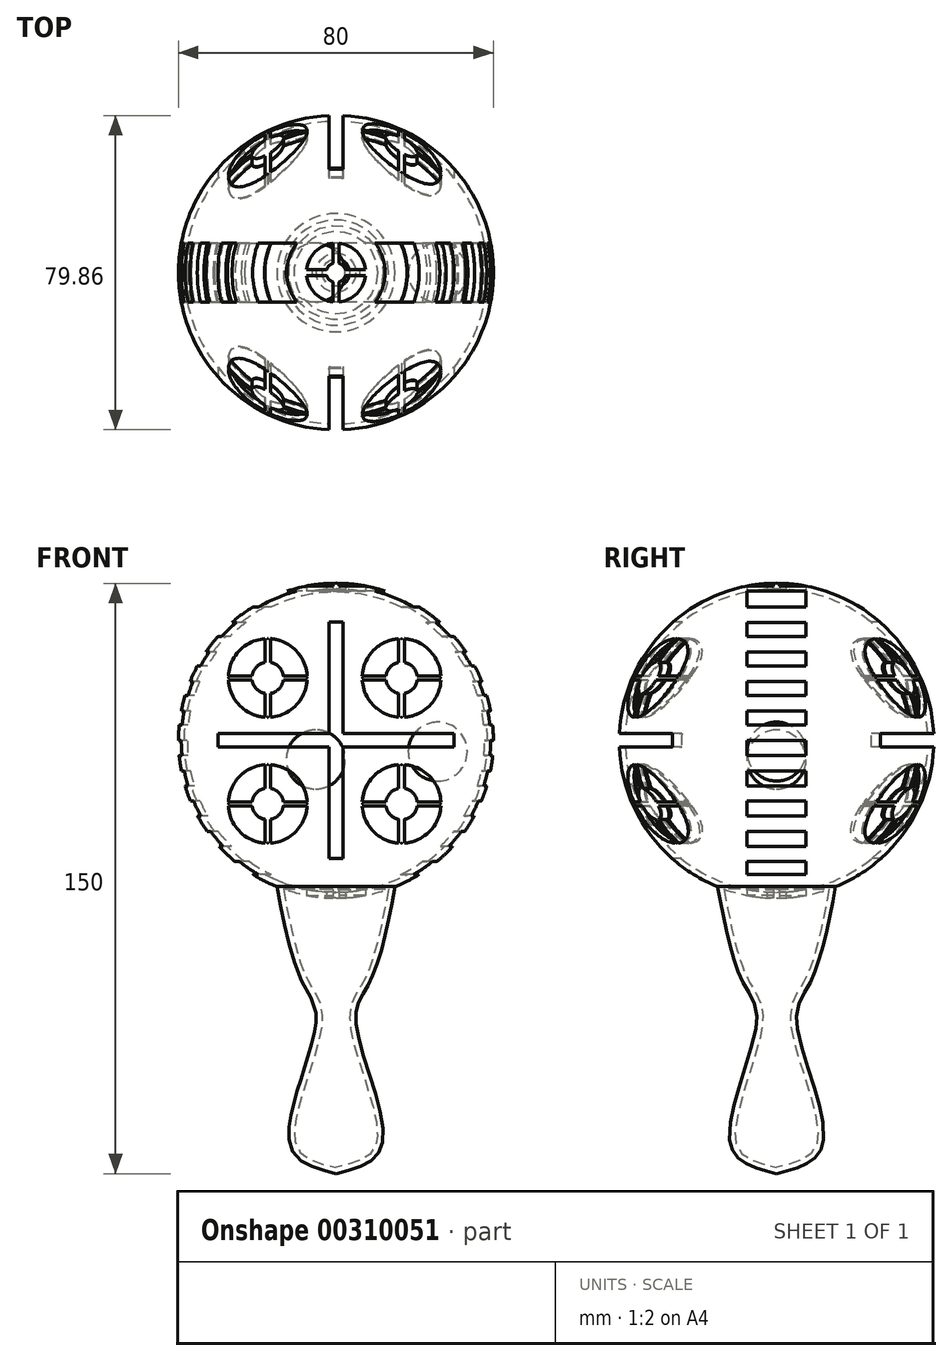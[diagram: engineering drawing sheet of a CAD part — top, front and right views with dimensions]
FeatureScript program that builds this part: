
annotation { "Feature Type Name" : "Feature", "Feature Type Description" : "" }
export const myFeature = defineFeature(function(context is Context, id is Id, definition is map)
    precondition{}
    {
        {
            var Q0;
            Q0=qCreatedBy(makeId("Front.planeOp"),FACE);
            var sketch = newSketch(context, id + "F0", { "sketchPlane" : qUnion([Q0])});
            skArc(sketch, "E0", {"start": v(0, 1.78) * mm, "mid": v(6.77, 2.36) * mm, "end": v(13.35, 4.08) * mm});
            skArc(sketch, "E1", {"start": v(0, 3.28) * mm, "mid": v(38.5, 41.78) * mm, "end": v(0, 80.28) * mm});
            skLineSegment(sketch, "E2", {"start": v(0, 81.78) * mm, "end": v(0, -68.22) * mm, "construction": true});
            skLineSegment(sketch, "E3", {"start": v(0, -68.22) * mm, "end": v(15, -68.22) * mm, "construction": true});
            skLineSegment(sketch, "E4", {"start": v(15, -68.22) * mm, "end": v(15, 6.32) * mm, "construction": true});
            skFitSpline(sketch, "E5", {"points": [v(15, 4.7) * mm, v(8.78, -19.12) * mm, v(5.03, -29.47) * mm, v(11.76, -60.64) * mm, v(0, -68.22) * mm], "startDerivative": vector(-18.71, -98) * mm, "endDerivative": vector(-75.4, -18.66) * mm});
            skFitSpline(sketch, "E6.0", {"points": [v(13.53, 4.98) * mm, v(13.14, 2.94) * mm, v(12.36, -1.13) * mm, v(11.34, -6) * mm, v(10.46, -9.63) * mm, v(9.77, -12.19) * mm, v(9.04, -14.55) * mm, v(8.4, -16.32) * mm, v(7.85, -17.6) * mm, v(7.43, -18.49) * mm, v(7, -19.31) * mm, v(6.4, -20.37) * mm, v(5.63, -21.64) * mm, v(4.74, -23.24) * mm, v(3.99, -25.03) * mm, v(3.6, -26.77) * mm, v(3.5, -28.31) * mm, v(3.52, -29.56) * mm, v(3.66, -30.9) * mm, v(3.98, -32.76) * mm, v(4.57, -35.27) * mm, v(5.51, -38.5) * mm, v(6.58, -41.88) * mm, v(7.68, -45.32) * mm, v(8.72, -48.72) * mm, v(9.61, -52) * mm, v(10.25, -55.06) * mm, v(10.55, -57.77) * mm, v(10.46, -59.63) * mm, v(10.19, -60.8) * mm, v(9.78, -61.81) * mm, v(9.05, -62.86) * mm, v(7.79, -63.92) * mm, v(6.14, -64.81) * mm, v(4.17, -65.55) * mm, v(1.98, -66.18) * mm, v(0.42, -66.57) * mm, v(-0.36, -66.76) * mm]});
            skLineSegment(sketch, "E7", {"start": v(0, -68.22) * mm, "end": v(0, 3.28) * mm});
            skArc(sketch, "E8.trimOffspring", {"start": v(15, 4.7) * mm, "mid": v(39.26, 49.42) * mm, "end": v(0, 81.78) * mm});
            skLineSegment(sketch, "E9", {"start": v(0, 81.78) * mm, "end": v(0, 80.28) * mm});
            skLineSegment(sketch, "E10", {"start": v(40, 41.95) * mm, "end": v(0, 41.78) * mm, "construction": true});
            skSolve(sketch);
        }
        {
            var Q0;
            {var subQ3=sQuery(id+"F0.wireOp",EDGE,"E0");Q0=makeQuery(id+"F0.imprint","IMPRINT",FACE,{"disambiguationData":[TD([[makeQuery(id+"F0.imprint","IMPRINT",EDGE,{"derivedFrom":subQ3}),1.0]])]});}
            var Q1;
            Q1=sQuery(id+"F0.wireOp",EDGE,"E2");
            revolve(context, id + "F1", {"entities" : qUnion([Q0]), "axis" : qUnion([Q1]), "revolveType" : RevolveType.FULL});
        }
        {
            var Q0;
            Q0=qCreatedBy(makeId("Front.planeOp"),FACE);
            var sketch = newSketch(context, id + "F2", { "sketchPlane" : qUnion([Q0])});
            skArc(sketch, "E11", {"start": v(15.94, 35.7) * mm, "mid": v(9.52, 32.73) * mm, "end": v(6.68, 26.25) * mm});
            skLineSegment(sketch, "E12", {"start": v(16.67, 35.73) * mm, "end": v(16.67, 35.7) * mm});
            skLineSegment(sketch, "E13", {"start": v(16.67, 15.73) * mm, "end": v(16.7, 15.76) * mm});
            skLineSegment(sketch, "E14", {"start": v(6.67, 25.73) * mm, "end": v(6.68, 25.74) * mm});
            skLineSegment(sketch, "E15", {"start": v(26.67, 25.73) * mm, "end": v(26.66, 25.74) * mm});
            skLineSegment(sketch, "E16", {"start": v(16.67, 15.73) * mm, "end": v(16.64, 15.76) * mm});
            skLineSegment(sketch, "E17.left", {"start": v(6.68, 25.72) * mm, "end": v(6.68, 25.74) * mm});
            skLineSegment(sketch, "E17.right", {"start": v(26.66, 25.72) * mm, "end": v(26.66, 25.74) * mm});
            skLineSegment(sketch, "E18.trimOffspring", {"start": v(6.68, 25.72) * mm, "end": v(6.67, 25.73) * mm});
            skLineSegment(sketch, "E19.trimOffspring", {"start": v(26.66, 25.72) * mm, "end": v(26.67, 25.73) * mm});
            skLineSegment(sketch, "E20.bottom", {"start": v(16.64, 15.76) * mm, "end": v(16.7, 15.76) * mm});
            skLineSegment(sketch, "E20.top", {"start": v(16.64, 35.7) * mm, "end": v(16.7, 35.7) * mm});
            skLineSegment(sketch, "E21.trimOffspring", {"start": v(16.64, 35.7) * mm, "end": v(16.67, 35.73) * mm});
            skLineSegment(sketch, "E22.trimOffspring", {"start": v(16.7, 35.7) * mm, "end": v(16.67, 35.73) * mm});
            skLineSegment(sketch, "E23.trimOffspring", {"start": v(16.67, 15.76) * mm, "end": v(16.67, 15.73) * mm});
            skLineSegment(sketch, "E24.bottom", {"start": v(-30, 40.15) * mm, "end": v(-1.75, 40.15) * mm});
            skLineSegment(sketch, "E24.top", {"start": v(-30, 43.65) * mm, "end": v(-1.75, 43.65) * mm});
            skLineSegment(sketch, "E24.left", {"start": v(-30, 40.15) * mm, "end": v(-30, 43.65) * mm});
            skLineSegment(sketch, "E24.right", {"start": v(30, 40.15) * mm, "end": v(30, 43.65) * mm});
            skPoint(sketch, "E24.middle", {"position": v(0, 41.9) * mm});
            skLineSegment(sketch, "E25.bottom", {"start": v(-1.75, 11.9) * mm, "end": v(1.75, 11.9) * mm});
            skLineSegment(sketch, "E25.top", {"start": v(-1.75, 71.9) * mm, "end": v(1.75, 71.9) * mm});
            skLineSegment(sketch, "E25.left", {"start": v(-1.75, 11.9) * mm, "end": v(-1.75, 40.15) * mm});
            skLineSegment(sketch, "E25.right", {"start": v(1.75, 11.9) * mm, "end": v(1.75, 40.15) * mm});
            skLineSegment(sketch, "E26.trimOffspring", {"start": v(1.75, 43.65) * mm, "end": v(1.75, 71.9) * mm});
            skLineSegment(sketch, "E27.trimOffspring", {"start": v(1.75, 43.65) * mm, "end": v(30, 43.65) * mm});
            skLineSegment(sketch, "E28.trimOffspring", {"start": v(1.75, 40.15) * mm, "end": v(30, 40.15) * mm});
            skLineSegment(sketch, "E29.trimOffspring", {"start": v(-1.75, 43.65) * mm, "end": v(-1.75, 71.9) * mm});
            skLineSegment(sketch, "E30.bottom", {"start": v(15.94, 37.7) * mm, "end": v(17.4, 37.7) * mm});
            skLineSegment(sketch, "E30.left", {"start": v(15.94, 35.7) * mm, "end": v(15.94, 29.66) * mm});
            skLineSegment(sketch, "E30.right", {"start": v(17.4, 35.7) * mm, "end": v(17.4, 29.66) * mm});
            skLineSegment(sketch, "E31.bottom", {"start": v(6.68, 26.25) * mm, "end": v(12.7, 26.25) * mm});
            skLineSegment(sketch, "E31.top", {"start": v(6.68, 25.21) * mm, "end": v(12.7, 25.21) * mm});
            skArc(sketch, "E32", {"start": v(12.7, 25.21) * mm, "mid": v(13.77, 22.98) * mm, "end": v(15.94, 21.8) * mm});
            skLineSegment(sketch, "E33.trimOffspring", {"start": v(20.64, 26.25) * mm, "end": v(26.66, 26.25) * mm});
            skLineSegment(sketch, "E34.trimOffspring", {"start": v(20.64, 25.21) * mm, "end": v(26.66, 25.21) * mm});
            skLineSegment(sketch, "E35.trimOffspring", {"start": v(17.4, 21.8) * mm, "end": v(17.4, 15.76) * mm});
            skLineSegment(sketch, "E36.trimOffspring", {"start": v(15.94, 21.8) * mm, "end": v(15.94, 15.76) * mm});
            skArc(sketch, "E37.trimOffspring", {"start": v(15.94, 29.66) * mm, "mid": v(13.77, 28.48) * mm, "end": v(12.7, 26.25) * mm});
            skArc(sketch, "E38.trimOffspring", {"start": v(20.64, 26.25) * mm, "mid": v(19.57, 28.48) * mm, "end": v(17.4, 29.66) * mm});
            skArc(sketch, "E39.trimOffspring", {"start": v(17.4, 21.8) * mm, "mid": v(19.57, 22.98) * mm, "end": v(20.64, 25.21) * mm});
            skArc(sketch, "E40.trimOffspring", {"start": v(26.66, 26.25) * mm, "mid": v(23.82, 32.73) * mm, "end": v(17.4, 35.7) * mm});
            skArc(sketch, "E41.trimOffspring", {"start": v(6.68, 25.21) * mm, "mid": v(9.52, 18.74) * mm, "end": v(15.94, 15.76) * mm});
            skArc(sketch, "E42.trimOffspring", {"start": v(17.4, 15.76) * mm, "mid": v(23.82, 18.74) * mm, "end": v(26.66, 25.21) * mm});
            skLineSegment(sketch, "E43.0.1.0", {"start": v(17.4, 67.7) * mm, "end": v(17.4, 61.66) * mm});
            skArc(sketch, "E43.0.1.1", {"start": v(17.4, 47.76) * mm, "mid": v(23.82, 50.74) * mm, "end": v(26.66, 57.21) * mm});
            skArc(sketch, "E43.0.1.2", {"start": v(6.68, 57.21) * mm, "mid": v(9.52, 50.74) * mm, "end": v(15.94, 47.76) * mm});
            skLineSegment(sketch, "E43.0.1.3", {"start": v(17.4, 53.8) * mm, "end": v(17.4, 47.76) * mm});
            skLineSegment(sketch, "E43.0.1.4", {"start": v(6.68, 58.25) * mm, "end": v(12.7, 58.25) * mm});
            skPoint(sketch, "E43.0.1.5", {"position": v(16.67, 57.73) * mm});
            skLineSegment(sketch, "E43.0.1.6", {"start": v(6.68, 57.21) * mm, "end": v(12.7, 57.21) * mm});
            skArc(sketch, "E43.0.1.7", {"start": v(15.94, 61.66) * mm, "mid": v(13.77, 60.48) * mm, "end": v(12.7, 58.25) * mm});
            skArc(sketch, "E43.0.1.8", {"start": v(15.94, 67.7) * mm, "mid": v(9.52, 64.73) * mm, "end": v(6.68, 58.25) * mm});
            skLineSegment(sketch, "E43.0.1.10", {"start": v(15.94, 67.7) * mm, "end": v(15.94, 61.66) * mm});
            skArc(sketch, "E43.0.1.11", {"start": v(26.66, 58.25) * mm, "mid": v(23.82, 64.73) * mm, "end": v(17.4, 67.7) * mm});
            skLineSegment(sketch, "E43.0.1.12", {"start": v(15.94, 53.8) * mm, "end": v(15.94, 47.76) * mm});
            skPoint(sketch, "E43.0.1.13", {"position": v(16.67, 57.73) * mm});
            skLineSegment(sketch, "E43.0.1.14", {"start": v(20.64, 58.25) * mm, "end": v(26.66, 58.25) * mm});
            skLineSegment(sketch, "E43.0.1.17", {"start": v(20.64, 57.21) * mm, "end": v(26.66, 57.21) * mm});
            skArc(sketch, "E43.0.1.18", {"start": v(17.4, 53.8) * mm, "mid": v(19.57, 54.98) * mm, "end": v(20.64, 57.21) * mm});
            skPoint(sketch, "E43.0.1.19", {"position": v(16.67, 57.73) * mm});
            skArc(sketch, "E43.0.1.20", {"start": v(12.7, 57.21) * mm, "mid": v(13.77, 54.98) * mm, "end": v(15.94, 53.8) * mm});
            skArc(sketch, "E43.0.1.21", {"start": v(20.64, 58.25) * mm, "mid": v(19.57, 60.48) * mm, "end": v(17.4, 61.66) * mm});
            skPoint(sketch, "E43.0.1.22", {"position": v(16.67, 57.73) * mm});
            skLineSegment(sketch, "E43.0.1.23", {"start": v(26.66, 57.72) * mm, "end": v(26.67, 57.73) * mm});
            skLineSegment(sketch, "E43.0.1.24", {"start": v(6.68, 57.72) * mm, "end": v(6.67, 57.73) * mm});
            skLineSegment(sketch, "E43.0.1.25", {"start": v(6.68, 57.72) * mm, "end": v(6.68, 57.74) * mm});
            skLineSegment(sketch, "E43.0.1.26", {"start": v(26.66, 57.72) * mm, "end": v(26.66, 57.74) * mm});
            skLineSegment(sketch, "E43.0.1.27", {"start": v(6.67, 57.73) * mm, "end": v(6.68, 57.74) * mm});
            skLineSegment(sketch, "E43.0.1.28", {"start": v(26.67, 57.73) * mm, "end": v(26.66, 57.74) * mm});
            skLineSegment(sketch, "E43.0.1.29", {"start": v(15.94, 45.75) * mm, "end": v(17.4, 45.75) * mm});
            skLineSegment(sketch, "E43.0.1.30", {"start": v(16.64, 67.7) * mm, "end": v(16.67, 67.73) * mm});
            skLineSegment(sketch, "E43.0.1.31", {"start": v(16.64, 47.76) * mm, "end": v(16.7, 47.76) * mm});
            skLineSegment(sketch, "E43.0.1.32", {"start": v(16.67, 47.73) * mm, "end": v(16.64, 47.76) * mm});
            skLineSegment(sketch, "E43.0.1.33", {"start": v(16.64, 67.7) * mm, "end": v(16.7, 67.7) * mm});
            skLineSegment(sketch, "E43.0.1.34", {"start": v(16.67, 47.73) * mm, "end": v(16.7, 47.76) * mm});
            skLineSegment(sketch, "E43.0.1.35", {"start": v(16.67, 67.73) * mm, "end": v(16.67, 67.7) * mm});
            skLineSegment(sketch, "E43.0.1.36", {"start": v(16.67, 47.76) * mm, "end": v(16.67, 47.73) * mm});
            skLineSegment(sketch, "E43.0.1.37", {"start": v(16.7, 67.7) * mm, "end": v(16.67, 67.73) * mm});
            skLineSegment(sketch, "E43.1.0.0", {"start": v(-16.6, 35.7) * mm, "end": v(-16.6, 29.66) * mm});
            skArc(sketch, "E43.1.0.1", {"start": v(-16.6, 15.76) * mm, "mid": v(-10.18, 18.74) * mm, "end": v(-7.34, 25.21) * mm});
            skArc(sketch, "E43.1.0.2", {"start": v(-27.32, 25.21) * mm, "mid": v(-24.48, 18.74) * mm, "end": v(-18.06, 15.76) * mm});
            skLineSegment(sketch, "E43.1.0.3", {"start": v(-16.6, 21.8) * mm, "end": v(-16.6, 15.76) * mm});
            skLineSegment(sketch, "E43.1.0.4", {"start": v(-27.32, 26.25) * mm, "end": v(-21.3, 26.25) * mm});
            skPoint(sketch, "E43.1.0.5", {"position": v(-17.33, 25.73) * mm});
            skLineSegment(sketch, "E43.1.0.6", {"start": v(-27.32, 25.21) * mm, "end": v(-21.3, 25.21) * mm});
            skArc(sketch, "E43.1.0.7", {"start": v(-18.06, 29.66) * mm, "mid": v(-20.23, 28.48) * mm, "end": v(-21.3, 26.25) * mm});
            skArc(sketch, "E43.1.0.8", {"start": v(-18.06, 35.7) * mm, "mid": v(-24.48, 32.73) * mm, "end": v(-27.32, 26.25) * mm});
            skLineSegment(sketch, "E43.1.0.10", {"start": v(-18.06, 35.7) * mm, "end": v(-18.06, 29.66) * mm});
            skArc(sketch, "E43.1.0.11", {"start": v(-7.34, 26.25) * mm, "mid": v(-10.18, 32.73) * mm, "end": v(-16.6, 35.7) * mm});
            skLineSegment(sketch, "E43.1.0.12", {"start": v(-18.06, 21.8) * mm, "end": v(-18.06, 15.76) * mm});
            skPoint(sketch, "E43.1.0.13", {"position": v(-17.33, 25.73) * mm});
            skLineSegment(sketch, "E43.1.0.14", {"start": v(-13.36, 26.25) * mm, "end": v(-7.34, 26.25) * mm});
            skLineSegment(sketch, "E43.1.0.17", {"start": v(-13.36, 25.21) * mm, "end": v(-7.34, 25.21) * mm});
            skArc(sketch, "E43.1.0.18", {"start": v(-16.6, 21.8) * mm, "mid": v(-14.43, 22.98) * mm, "end": v(-13.36, 25.21) * mm});
            skPoint(sketch, "E43.1.0.19", {"position": v(-17.33, 25.73) * mm});
            skArc(sketch, "E43.1.0.20", {"start": v(-21.3, 25.21) * mm, "mid": v(-20.23, 22.98) * mm, "end": v(-18.06, 21.8) * mm});
            skArc(sketch, "E43.1.0.21", {"start": v(-13.36, 26.25) * mm, "mid": v(-14.43, 28.48) * mm, "end": v(-16.6, 29.66) * mm});
            skPoint(sketch, "E43.1.0.22", {"position": v(-17.33, 25.73) * mm});
            skLineSegment(sketch, "E43.1.0.23", {"start": v(-7.34, 25.72) * mm, "end": v(-7.33, 25.73) * mm});
            skLineSegment(sketch, "E43.1.0.24", {"start": v(-27.32, 25.72) * mm, "end": v(-27.33, 25.73) * mm});
            skLineSegment(sketch, "E43.1.0.25", {"start": v(-27.32, 25.72) * mm, "end": v(-27.32, 25.74) * mm});
            skLineSegment(sketch, "E43.1.0.26", {"start": v(-7.34, 25.72) * mm, "end": v(-7.34, 25.74) * mm});
            skLineSegment(sketch, "E43.1.0.27", {"start": v(-27.33, 25.73) * mm, "end": v(-27.32, 25.74) * mm});
            skLineSegment(sketch, "E43.1.0.28", {"start": v(-7.33, 25.73) * mm, "end": v(-7.34, 25.74) * mm});
            skLineSegment(sketch, "E43.1.0.30", {"start": v(-17.36, 35.7) * mm, "end": v(-17.33, 35.73) * mm});
            skLineSegment(sketch, "E43.1.0.31", {"start": v(-17.36, 15.76) * mm, "end": v(-17.3, 15.76) * mm});
            skLineSegment(sketch, "E43.1.0.32", {"start": v(-17.33, 15.73) * mm, "end": v(-17.36, 15.76) * mm});
            skLineSegment(sketch, "E43.1.0.33", {"start": v(-17.36, 35.7) * mm, "end": v(-17.3, 35.7) * mm});
            skLineSegment(sketch, "E43.1.0.34", {"start": v(-17.33, 15.73) * mm, "end": v(-17.3, 15.76) * mm});
            skLineSegment(sketch, "E43.1.0.35", {"start": v(-17.33, 35.73) * mm, "end": v(-17.33, 35.7) * mm});
            skLineSegment(sketch, "E43.1.0.36", {"start": v(-17.33, 15.76) * mm, "end": v(-17.33, 15.73) * mm});
            skLineSegment(sketch, "E43.1.0.37", {"start": v(-17.3, 35.7) * mm, "end": v(-17.33, 35.73) * mm});
            skLineSegment(sketch, "E43.1.1.0", {"start": v(-16.6, 67.7) * mm, "end": v(-16.6, 61.66) * mm});
            skArc(sketch, "E43.1.1.1", {"start": v(-16.6, 47.76) * mm, "mid": v(-10.18, 50.74) * mm, "end": v(-7.34, 57.21) * mm});
            skArc(sketch, "E43.1.1.2", {"start": v(-27.32, 57.21) * mm, "mid": v(-24.48, 50.74) * mm, "end": v(-18.06, 47.76) * mm});
            skLineSegment(sketch, "E43.1.1.3", {"start": v(-16.6, 53.8) * mm, "end": v(-16.6, 47.76) * mm});
            skLineSegment(sketch, "E43.1.1.4", {"start": v(-27.32, 58.25) * mm, "end": v(-21.3, 58.25) * mm});
            skPoint(sketch, "E43.1.1.5", {"position": v(-17.33, 57.73) * mm});
            skLineSegment(sketch, "E43.1.1.6", {"start": v(-27.32, 57.21) * mm, "end": v(-21.3, 57.21) * mm});
            skArc(sketch, "E43.1.1.7", {"start": v(-18.06, 61.66) * mm, "mid": v(-20.23, 60.48) * mm, "end": v(-21.3, 58.25) * mm});
            skArc(sketch, "E43.1.1.8", {"start": v(-18.06, 67.7) * mm, "mid": v(-24.48, 64.73) * mm, "end": v(-27.32, 58.25) * mm});
            skLineSegment(sketch, "E43.1.1.10", {"start": v(-18.06, 67.7) * mm, "end": v(-18.06, 61.66) * mm});
            skArc(sketch, "E43.1.1.11", {"start": v(-7.34, 58.25) * mm, "mid": v(-10.18, 64.73) * mm, "end": v(-16.6, 67.7) * mm});
            skLineSegment(sketch, "E43.1.1.12", {"start": v(-18.06, 53.8) * mm, "end": v(-18.06, 47.76) * mm});
            skPoint(sketch, "E43.1.1.13", {"position": v(-17.33, 57.73) * mm});
            skLineSegment(sketch, "E43.1.1.14", {"start": v(-13.36, 58.25) * mm, "end": v(-7.34, 58.25) * mm});
            skLineSegment(sketch, "E43.1.1.17", {"start": v(-13.36, 57.21) * mm, "end": v(-7.34, 57.21) * mm});
            skArc(sketch, "E43.1.1.18", {"start": v(-16.6, 53.8) * mm, "mid": v(-14.43, 54.98) * mm, "end": v(-13.36, 57.21) * mm});
            skPoint(sketch, "E43.1.1.19", {"position": v(-17.33, 57.73) * mm});
            skArc(sketch, "E43.1.1.20", {"start": v(-21.3, 57.21) * mm, "mid": v(-20.23, 54.98) * mm, "end": v(-18.06, 53.8) * mm});
            skArc(sketch, "E43.1.1.21", {"start": v(-13.36, 58.25) * mm, "mid": v(-14.43, 60.48) * mm, "end": v(-16.6, 61.66) * mm});
            skPoint(sketch, "E43.1.1.22", {"position": v(-17.33, 57.73) * mm});
            skLineSegment(sketch, "E43.1.1.23", {"start": v(-7.34, 57.72) * mm, "end": v(-7.33, 57.73) * mm});
            skLineSegment(sketch, "E43.1.1.24", {"start": v(-27.32, 57.72) * mm, "end": v(-27.33, 57.73) * mm});
            skLineSegment(sketch, "E43.1.1.25", {"start": v(-27.32, 57.72) * mm, "end": v(-27.32, 57.74) * mm});
            skLineSegment(sketch, "E43.1.1.26", {"start": v(-7.34, 57.72) * mm, "end": v(-7.34, 57.74) * mm});
            skLineSegment(sketch, "E43.1.1.27", {"start": v(-27.33, 57.73) * mm, "end": v(-27.32, 57.74) * mm});
            skLineSegment(sketch, "E43.1.1.28", {"start": v(-7.33, 57.73) * mm, "end": v(-7.34, 57.74) * mm});
            skLineSegment(sketch, "E43.1.1.30", {"start": v(-17.36, 67.7) * mm, "end": v(-17.33, 67.73) * mm});
            skLineSegment(sketch, "E43.1.1.31", {"start": v(-17.36, 47.76) * mm, "end": v(-17.3, 47.76) * mm});
            skLineSegment(sketch, "E43.1.1.32", {"start": v(-17.33, 47.73) * mm, "end": v(-17.36, 47.76) * mm});
            skLineSegment(sketch, "E43.1.1.33", {"start": v(-17.36, 67.7) * mm, "end": v(-17.3, 67.7) * mm});
            skLineSegment(sketch, "E43.1.1.34", {"start": v(-17.33, 47.73) * mm, "end": v(-17.3, 47.76) * mm});
            skLineSegment(sketch, "E43.1.1.35", {"start": v(-17.33, 67.73) * mm, "end": v(-17.33, 67.7) * mm});
            skLineSegment(sketch, "E43.1.1.36", {"start": v(-17.33, 47.76) * mm, "end": v(-17.33, 47.73) * mm});
            skLineSegment(sketch, "E43.1.1.37", {"start": v(-17.3, 67.7) * mm, "end": v(-17.33, 67.73) * mm});
            skLineSegment(sketch, "E43.direction1", {"start": v(15.94, 13.75) * mm, "end": v(-18.06, 13.75) * mm, "construction": true});
            skLineSegment(sketch, "E43.direction2", {"start": v(15.94, 13.75) * mm, "end": v(15.94, 45.75) * mm, "construction": true});
            skSolve(sketch);
        }
        {
            var Q0;
            Q0 = qSketchRegion(id + "F2", true);
            extrude(context, id + "F3", {"entities" : qUnion([Q0]), "operationType" : NewBodyOperationType.REMOVE, "endBound" : BoundingType.SYMMETRIC, "oppositeDirection" : true, "depth" : 85 * mm});
        }
        {
            var Q0;
            Q0=qCreatedBy(makeId("Right.planeOp"),FACE);
            var sketch = newSketch(context, id + "F4", { "sketchPlane" : qUnion([Q0])});
            skLineSegment(sketch, "E44.bottom", {"start": v(-7.5, 7.79) * mm, "end": v(7.5, 7.79) * mm});
            skLineSegment(sketch, "E44.top", {"start": v(-7.5, 79.79) * mm, "end": v(7.5, 79.79) * mm});
            skLineSegment(sketch, "E44.left", {"start": v(-7.5, 7.79) * mm, "end": v(-7.5, 11.05) * mm});
            skLineSegment(sketch, "E44.right", {"start": v(7.5, 7.79) * mm, "end": v(7.5, 11.05) * mm});
            skPoint(sketch, "E44.middle", {"position": v(0, 43.79) * mm});
            skLineSegment(sketch, "E45.bottom", {"start": v(-7.5, 41.85) * mm, "end": v(7.5, 41.85) * mm});
            skLineSegment(sketch, "E45.top", {"start": v(-7.5, 45.73) * mm, "end": v(7.5, 45.73) * mm});
            skLineSegment(sketch, "E46.0.1.0", {"start": v(-7.5, 53.23) * mm, "end": v(7.5, 53.23) * mm});
            skLineSegment(sketch, "E46.0.1.1", {"start": v(-7.5, 49.35) * mm, "end": v(7.5, 49.35) * mm});
            skLineSegment(sketch, "E46.0.2.0", {"start": v(-7.5, 60.73) * mm, "end": v(7.5, 60.73) * mm});
            skLineSegment(sketch, "E46.0.2.1", {"start": v(-7.5, 56.85) * mm, "end": v(7.5, 56.85) * mm});
            skLineSegment(sketch, "E46.0.3.0", {"start": v(-7.5, 68.23) * mm, "end": v(7.5, 68.23) * mm});
            skLineSegment(sketch, "E46.0.3.1", {"start": v(-7.5, 64.35) * mm, "end": v(7.5, 64.35) * mm});
            skLineSegment(sketch, "E46.0.4.0", {"start": v(-7.5, 75.73) * mm, "end": v(7.5, 75.73) * mm});
            skLineSegment(sketch, "E46.0.4.1", {"start": v(-7.5, 71.85) * mm, "end": v(7.5, 71.85) * mm});
            skLineSegment(sketch, "E46.direction2", {"start": v(-7.5, 45.73) * mm, "end": v(-7.5, 49.35) * mm, "construction": true});
            skLineSegment(sketch, "E47.0.1.0", {"start": v(-7.5, 38.03) * mm, "end": v(7.5, 38.03) * mm});
            skLineSegment(sketch, "E47.0.1.1", {"start": v(-7.5, 34.15) * mm, "end": v(7.5, 34.15) * mm});
            skLineSegment(sketch, "E47.0.2.0", {"start": v(-7.5, 30.33) * mm, "end": v(7.5, 30.33) * mm});
            skLineSegment(sketch, "E47.0.2.1", {"start": v(-7.5, 26.45) * mm, "end": v(7.5, 26.45) * mm});
            skLineSegment(sketch, "E47.0.3.0", {"start": v(-7.5, 22.63) * mm, "end": v(7.5, 22.63) * mm});
            skLineSegment(sketch, "E47.0.3.1", {"start": v(-7.5, 18.75) * mm, "end": v(7.5, 18.75) * mm});
            skLineSegment(sketch, "E47.0.4.0", {"start": v(-7.5, 14.93) * mm, "end": v(7.5, 14.93) * mm});
            skLineSegment(sketch, "E47.0.4.1", {"start": v(-7.5, 11.05) * mm, "end": v(7.5, 11.05) * mm});
            skLineSegment(sketch, "E47.direction2", {"start": v(-7.5, 41.85) * mm, "end": v(-7.5, 38.03) * mm, "construction": true});
            skLineSegment(sketch, "E48.trimOffspring", {"start": v(7.5, 75.73) * mm, "end": v(7.5, 79.79) * mm});
            skLineSegment(sketch, "E49.trimOffspring", {"start": v(-7.5, 75.73) * mm, "end": v(-7.5, 79.79) * mm});
            skLineSegment(sketch, "E50.trimOffspring", {"start": v(7.5, 68.23) * mm, "end": v(7.5, 71.85) * mm});
            skLineSegment(sketch, "E51.trimOffspring", {"start": v(-7.5, 68.23) * mm, "end": v(-7.5, 71.85) * mm});
            skLineSegment(sketch, "E52.trimOffspring", {"start": v(7.5, 60.73) * mm, "end": v(7.5, 64.35) * mm});
            skLineSegment(sketch, "E53.trimOffspring", {"start": v(-7.5, 60.73) * mm, "end": v(-7.5, 64.35) * mm});
            skLineSegment(sketch, "E54.trimOffspring", {"start": v(7.5, 53.23) * mm, "end": v(7.5, 56.85) * mm});
            skLineSegment(sketch, "E55.trimOffspring", {"start": v(-7.5, 53.23) * mm, "end": v(-7.5, 56.85) * mm});
            skLineSegment(sketch, "E56.trimOffspring", {"start": v(7.5, 45.73) * mm, "end": v(7.5, 49.35) * mm});
            skLineSegment(sketch, "E57.trimOffspring", {"start": v(7.5, 38.03) * mm, "end": v(7.5, 41.85) * mm});
            skLineSegment(sketch, "E58.trimOffspring", {"start": v(-7.5, 45.73) * mm, "end": v(-7.5, 49.35) * mm});
            skLineSegment(sketch, "E59.trimOffspring", {"start": v(-7.5, 38.03) * mm, "end": v(-7.5, 41.85) * mm});
            skLineSegment(sketch, "E60.trimOffspring", {"start": v(-7.5, 30.33) * mm, "end": v(-7.5, 34.15) * mm});
            skLineSegment(sketch, "E61.trimOffspring", {"start": v(7.5, 30.33) * mm, "end": v(7.5, 34.15) * mm});
            skLineSegment(sketch, "E62.trimOffspring", {"start": v(7.5, 22.63) * mm, "end": v(7.5, 26.45) * mm});
            skLineSegment(sketch, "E63.trimOffspring", {"start": v(-7.5, 22.63) * mm, "end": v(-7.5, 26.45) * mm});
            skLineSegment(sketch, "E64.trimOffspring", {"start": v(7.5, 14.93) * mm, "end": v(7.5, 18.75) * mm});
            skLineSegment(sketch, "E65.trimOffspring", {"start": v(-7.5, 14.93) * mm, "end": v(-7.5, 18.75) * mm});
            skSolve(sketch);
        }
        {
            var Q0;
            Q0 = qSketchRegion(id + "F4", true);
            extrude(context, id + "F5", {"entities" : qUnion([Q0]), "operationType" : NewBodyOperationType.REMOVE, "endBound" : BoundingType.SYMMETRIC, "depth" : 85 * mm});
        }
        {
            var Q0;
            Q0=qCreatedBy(makeId("Top.planeOp"),FACE);
            var sketch = newSketch(context, id + "F6", { "sketchPlane" : qUnion([Q0])});
            skArc(sketch, "E66", {"start": v(-7.46, -0.78) * mm, "mid": v(-5.3, -5.3) * mm, "end": v(-0.77, -7.46) * mm});
            skArc(sketch, "E67", {"start": v(-0.77, 2.38) * mm, "mid": v(-1.76, 1.77) * mm, "end": v(-2.38, 0.78) * mm});
            skLineSegment(sketch, "E68.left", {"start": v(-0.77, -7.46) * mm, "end": v(-0.77, -2.38) * mm});
            skLineSegment(sketch, "E68.right", {"start": v(0.77, -7.46) * mm, "end": v(0.77, -2.38) * mm});
            skLineSegment(sketch, "E69.bottom", {"start": v(-7.46, -0.78) * mm, "end": v(-2.38, -0.78) * mm});
            skLineSegment(sketch, "E69.top", {"start": v(-7.46, 0.78) * mm, "end": v(-2.38, 0.78) * mm});
            skLineSegment(sketch, "E70.trimOffspring", {"start": v(0.77, 2.38) * mm, "end": v(0.77, 7.46) * mm});
            skLineSegment(sketch, "E71.trimOffspring", {"start": v(-0.77, 2.38) * mm, "end": v(-0.77, 7.46) * mm});
            skLineSegment(sketch, "E72.trimOffspring", {"start": v(2.38, 0.78) * mm, "end": v(7.46, 0.78) * mm});
            skLineSegment(sketch, "E73.trimOffspring", {"start": v(2.38, -0.78) * mm, "end": v(7.46, -0.78) * mm});
            skArc(sketch, "E74.trimOffspring", {"start": v(-2.38, -0.78) * mm, "mid": v(-1.76, -1.77) * mm, "end": v(-0.77, -2.38) * mm});
            skArc(sketch, "E75.trimOffspring", {"start": v(0.77, -2.38) * mm, "mid": v(1.76, -1.77) * mm, "end": v(2.38, -0.78) * mm});
            skArc(sketch, "E76.trimOffspring", {"start": v(7.46, 0.78) * mm, "mid": v(5.3, 5.3) * mm, "end": v(0.77, 7.46) * mm});
            skArc(sketch, "E77.trimOffspring", {"start": v(-0.77, 7.46) * mm, "mid": v(-5.3, 5.3) * mm, "end": v(-7.46, 0.78) * mm});
            skArc(sketch, "E78.trimOffspring", {"start": v(0.77, -7.46) * mm, "mid": v(5.3, -5.3) * mm, "end": v(7.46, -0.78) * mm});
            skArc(sketch, "E79.trimOffspring", {"start": v(2.38, 0.78) * mm, "mid": v(1.76, 1.77) * mm, "end": v(0.77, 2.38) * mm});
            skSolve(sketch);
        }
        {
            var Q0;
            Q0 = qSketchRegion(id + "F6", true);
            extrude(context, id + "F7", {"entities" : qUnion([Q0]), "operationType" : NewBodyOperationType.REMOVE, "depth" : 85 * mm});
        }
        {
            var Q0;
            Q0=qCreatedBy(makeId("Front.planeOp"),FACE);
            var sketch = newSketch(context, id + "F8", { "sketchPlane" : qUnion([Q0])});
            skArc(sketch, "E80", {"start": v(-5.13, 44.53) * mm, "mid": v(-12.63, 37.03) * mm, "end": v(-5.13, 29.53) * mm});
            skArc(sketch, "E81", {"start": v(25.86, 46.51) * mm, "mid": v(18.36, 39.01) * mm, "end": v(25.86, 31.51) * mm});
            skLineSegment(sketch, "E82", {"start": v(25.86, 39.01) * mm, "end": v(25.86, 46.51) * mm});
            skLineSegment(sketch, "E83", {"start": v(25.86, 46.51) * mm, "end": v(25.86, 31.51) * mm});
            skLineSegment(sketch, "E84", {"start": v(-5.13, 37.03) * mm, "end": v(-5.13, 44.53) * mm});
            skLineSegment(sketch, "E85", {"start": v(-5.13, 44.53) * mm, "end": v(-5.13, 29.53) * mm});
            skSolve(sketch);
        }
        {
            var Q0;
            {var subQ0=sQuery(id+"F8.wireOp",EDGE,"E80");Q0=makeQuery(id+"F8.imprint","IMPRINT",FACE,{"disambiguationData":[TD([[makeQuery(id+"F8.imprint","IMPRINT",EDGE,{"derivedFrom":subQ0}),1.0]])]});}
            var Q1;
            Q1=sQuery(id+"F8.wireOp",EDGE,"E85");
            revolve(context, id + "F9", {"entities" : qUnion([Q0]), "axis" : qUnion([Q1]), "revolveType" : RevolveType.FULL});
        }
        {
            var Q0;
            {var subQ0=sQuery(id+"F8.wireOp",EDGE,"E81");Q0=makeQuery(id+"F8.imprint","IMPRINT",FACE,{"disambiguationData":[TD([[makeQuery(id+"F8.imprint","IMPRINT",EDGE,{"derivedFrom":subQ0}),1.0]])]});}
            var Q1;
            Q1=sQuery(id+"F8.wireOp",EDGE,"E83");
            revolve(context, id + "F10", {"entities" : qUnion([Q0]), "axis" : qUnion([Q1]), "revolveType" : RevolveType.FULL});
        }
    });
